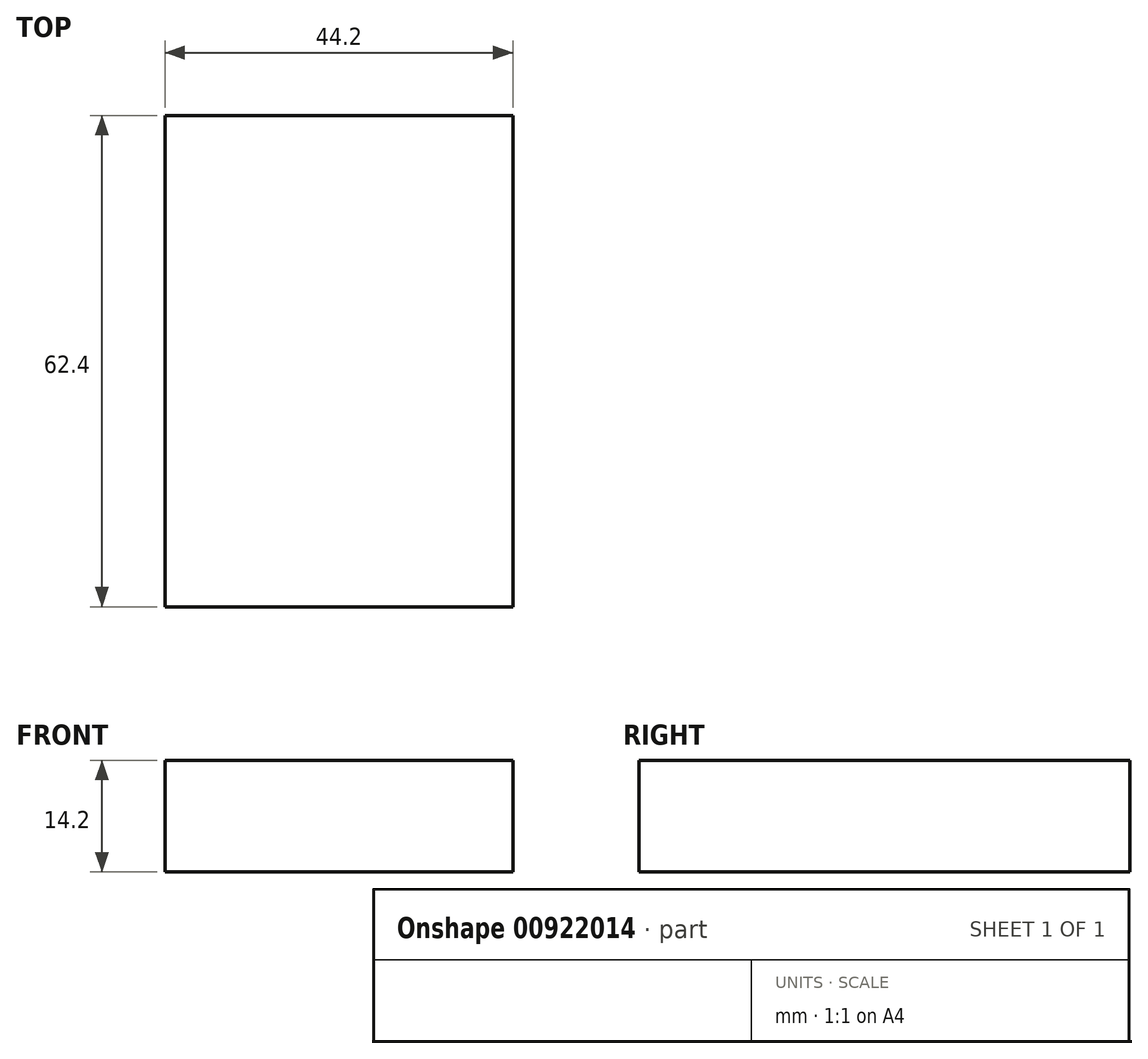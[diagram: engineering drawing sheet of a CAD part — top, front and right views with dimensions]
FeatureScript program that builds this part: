
annotation { "Feature Type Name" : "Feature", "Feature Type Description" : "" }
export const myFeature = defineFeature(function(context is Context, id is Id, definition is map)
    precondition{}
    {
        {
            var Q0;
            Q0=qCreatedBy(makeId("Top.planeOp"),FACE);
            var sketch = newSketch(context, id + "F0", { "sketchPlane" : qUnion([Q0])});
            skLineSegment(sketch, "E0.bottom", {"start": v(0, 0) * mm, "end": v(44.2, 0) * mm});
            skLineSegment(sketch, "E0.top", {"start": v(0, 62.4) * mm, "end": v(44.2, 62.4) * mm});
            skLineSegment(sketch, "E0.left", {"start": v(0, 0) * mm, "end": v(0, 62.4) * mm});
            skLineSegment(sketch, "E0.right", {"start": v(44.2, 0) * mm, "end": v(44.2, 62.4) * mm});
            skSolve(sketch);
        }
        {
            var Q0;
            Q0 = qSketchRegion(id + "F0", true);
            extrude(context, id + "F1", {"entities" : qUnion([Q0]), "depth" : 14.2 * mm, "offsetDistance" : 25 * mm});
        }
    });
